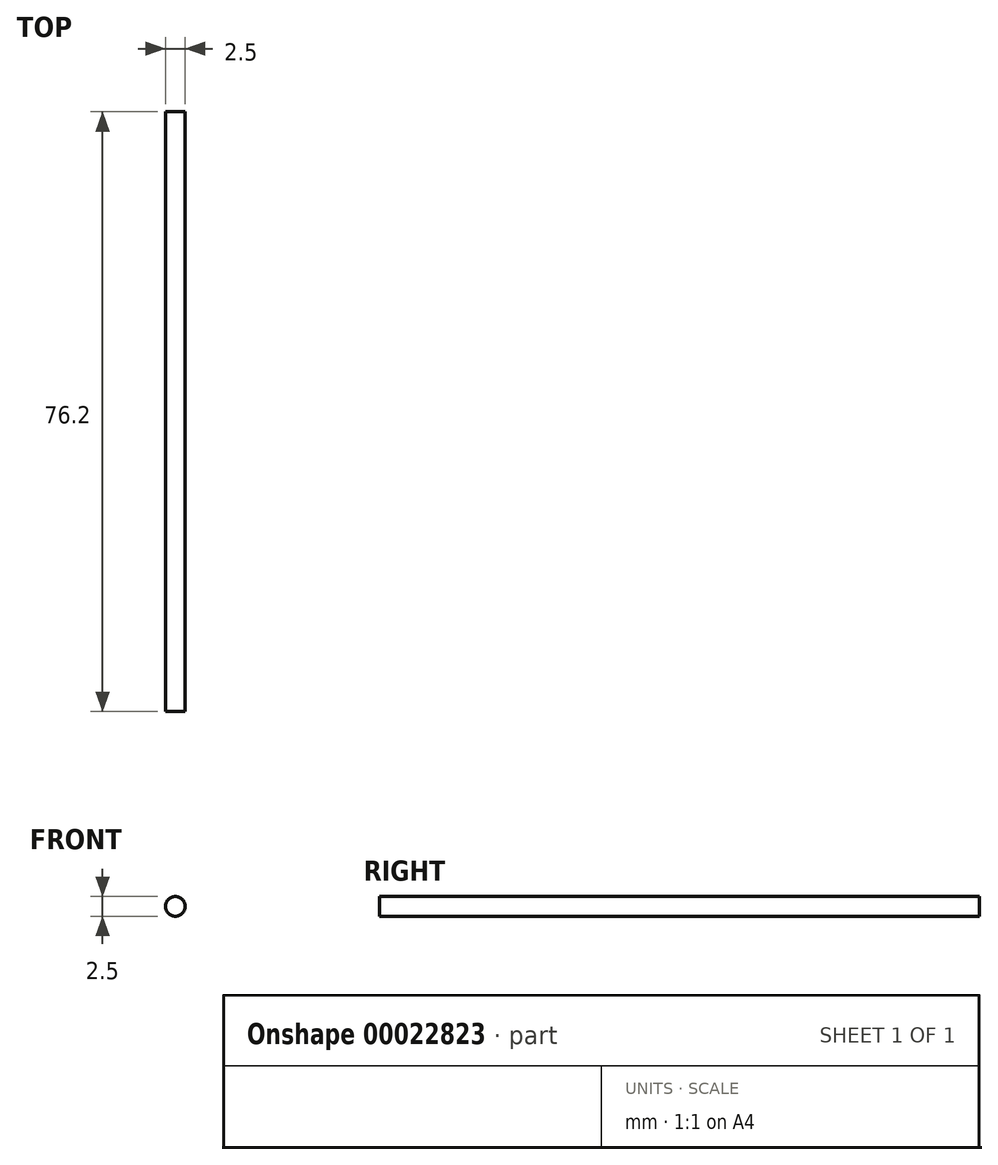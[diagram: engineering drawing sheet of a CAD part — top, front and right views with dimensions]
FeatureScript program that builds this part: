
annotation { "Feature Type Name" : "Feature", "Feature Type Description" : "" }
export const myFeature = defineFeature(function(context is Context, id is Id, definition is map)
    precondition{}
    {
        {
            var Q0;
            Q0=qCreatedBy(makeId("Front.planeOp"),FACE);
            var sketch = newSketch(context, id + "F0", { "sketchPlane" : qUnion([Q0])});
            skCircle(sketch, "E0", {"center": v(34.93, 11.05) * mm, "radius": 1.25 * mm});
            skSolve(sketch);
        }
        {
            var Q0;
            Q0 = qSketchRegion(id + "F0", true);
            extrude(context, id + "F1", {"entities" : qUnion([Q0]), "endBound" : BoundingType.SYMMETRIC, "depth" : 76.2 * mm});
        }
    });
